# Revit family: Seating-LAMMHULTS-TRIOO-I
name_source: partatom
category: Furniture
revit_build: Autodesk Revit 2018 (Build: 20181015_0930(x64)
units: mm (PartAtom-declared; Revit-internal decimal feet)

## family parameters
Always vertical = Yes
Cut with Voids When Loaded = No
OmniClass Number = 23.40.20.00
OmniClass Title = General Furniture and Specialties
Room Calculation Point = No
Shared = No
Work Plane-Based = No

## types (4) — shared parameters
Assembly Code = E2020
Depth = 540 mm  [stored 1.77165 ft]
Description = *Please enter mtrl description here for use in mto*
Height = 790 mm  [stored 2.59186 ft]
Keynote = 46.B
Manufacturer = LAMMHULTS
Model = TRIOO
URL = www.lammhults.se
Weight = 4.5kg
Width = 520 mm  [stored 1.70604 ft]

## per-type parameters (varying)
| type | Back Material | Frame Material | Seat Bottom Material | Seat Material |
| Black w Black Seat and Back | Wood - Imprint - Black | Metal - Black - Matte | Wood - Imprint - Black | Wood - Imprint - Black |
| Chrome w Black Leather Seat and Oak Back | Wood - Veneer - Fineline Oak | Metal - Chrome - Polished | Fabric - Grey Woven | Leather - Rustical - Black |
| Chrome w Ash Seat and Back | Wood - Veneer - Ash | Metal - Chrome - Polished | Fabric - Grey Woven | Wood - Veneer - Ash |
| Chrome w Oak Seat and Back | Wood - Veneer - Fineline Oak | Metal - Chrome - Polished | Fabric - Grey Woven | Wood - Veneer - Fineline Oak |

note: [stored X ft] marks values corroborated as IEEE doubles in the binary element streams (Revit-internal decimal feet)

## geometry (parser evidence)
native form markers: Blend x5, Sweep x1
no freeform markers — native parametric forms only
